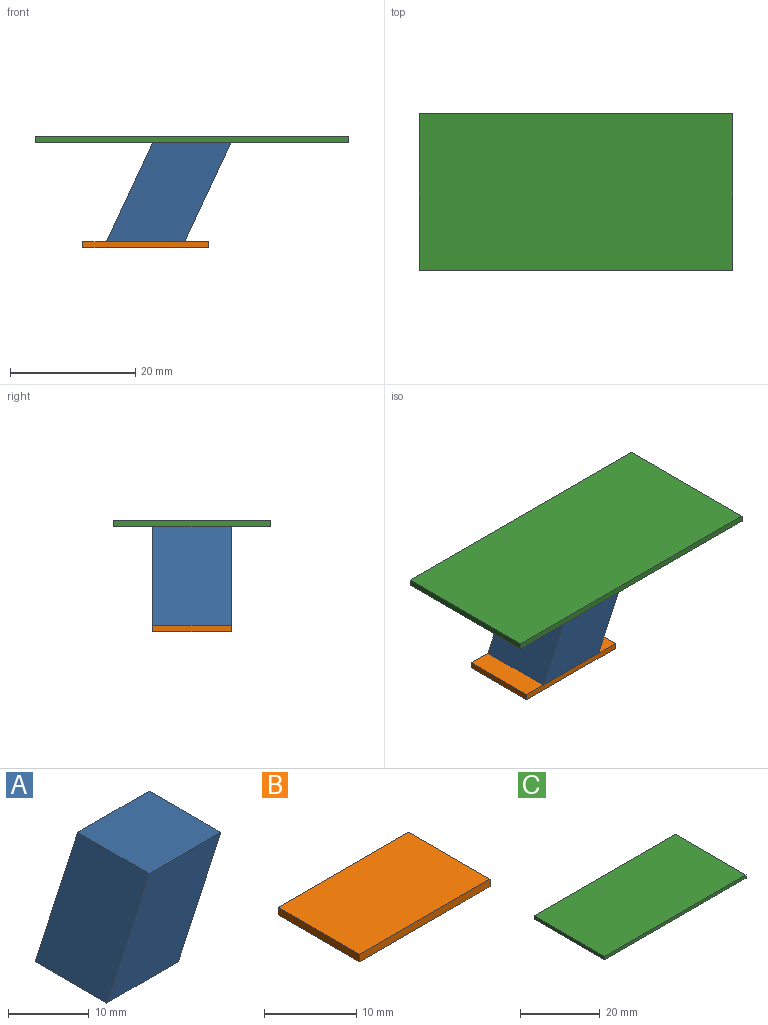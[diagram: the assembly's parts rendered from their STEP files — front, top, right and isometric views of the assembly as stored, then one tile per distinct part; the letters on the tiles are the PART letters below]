
ASSEMBLY  parts=3 mates=2
PART A: 6 faces, bbox 19.9x12.5x15.9 mm
  f0: plane 12.5x12.5mm, normal (0,0,-1), area 156.2mm2, adj f1,f3,f4,f5
  f1: plane 15.85x12.5mm, normal (0.91,0,-0.42), area 218.8mm2, adj f0,f2,f4,f5
  f2: plane 12.5x12.5mm, normal (0,0,1), area 156.2mm2, adj f1,f3,f4,f5
  f3: plane 15.85x12.5mm, normal (-0.91,0,0.42), area 218.8mm2, adj f0,f2,f4,f5
  f4: plane 19.91x15.85mm, normal (0,-1,0), area 198.1mm2, adj f0,f1,f2,f3
  f5: plane 19.91x15.85mm, normal (0,1,0), area 198.1mm2, adj f0,f1,f2,f3
PART B: 6 faces, bbox 20x12.5x1 mm
  f0: plane 12.5x1mm, normal (1,0,0), area 12.5mm2, adj f1,f3,f4,f5
  f1: plane 20x1mm, normal (0,1,0), area 20mm2, adj f0,f2,f4,f5
  f2: plane 12.5x1mm, normal (-1,0,0), area 12.5mm2, adj f1,f3,f4,f5
  f3: plane 20x1mm, normal (0,-1,0), area 20mm2, adj f0,f2,f4,f5
  f4: plane 20x12.5mm, normal (0,0,1), area 250mm2, adj f0,f1,f2,f3
  f5: plane 20x12.5mm, normal (0,0,-1), area 250mm2, adj f0,f1,f2,f3
PART C: 6 faces, bbox 50x25x1 mm
  f0: plane 25x1mm, normal (1,0,0), area 25mm2, adj f1,f3,f4,f5
  f1: plane 50x1mm, normal (0,1,0), area 50mm2, adj f0,f2,f4,f5
  f2: plane 25x1mm, normal (-1,0,0), area 25mm2, adj f1,f3,f4,f5
  f3: plane 50x1mm, normal (0,-1,0), area 50mm2, adj f0,f2,f4,f5
  f4: plane 50x25mm, normal (0,0,1), area 1250mm2, adj f0,f1,f2,f3
  f5: plane 50x25mm, normal (0,0,-1), area 1250mm2, adj f0,f1,f2,f3
PLACE A t=(3.97,10.04,19.66)mm
PLACE B t=(1.57,-2.46,-0.37)mm fixed
PLACE C t=(23.98,-8.71,16.48)mm
MATE fastened A.f0 <-> B.f4  axis (0,0,-1) through (-8.43,3.79,0.63)mm
MATE fastened C.f5 <-> A.f2  axis (0,0,-1) through (-1.02,3.79,16.48)mm
